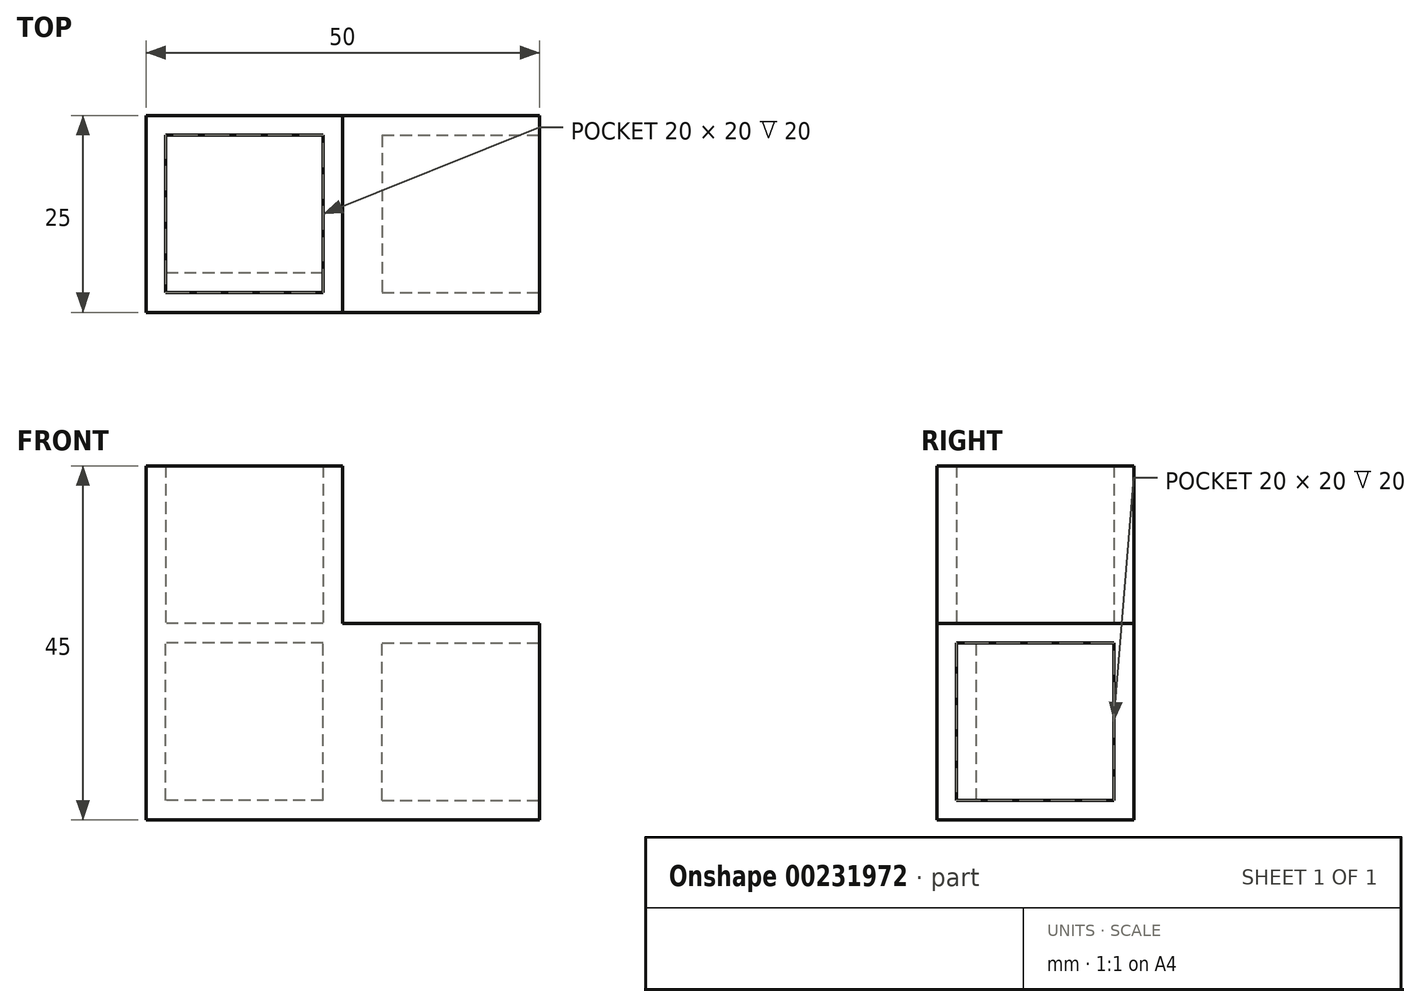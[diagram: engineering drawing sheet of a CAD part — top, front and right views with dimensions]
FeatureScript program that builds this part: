
annotation { "Feature Type Name" : "Feature", "Feature Type Description" : "" }
export const myFeature = defineFeature(function(context is Context, id is Id, definition is map)
    precondition{}
    {
        {
            var Q0;
            Q0=qCreatedBy(makeId("Top.planeOp"),FACE);
            var sketch = newSketch(context, id + "F0", { "sketchPlane" : qUnion([Q0])});
            skLineSegment(sketch, "E0.top", {"start": v(0, 30) * mm, "end": v(-25, 30) * mm});
            skLineSegment(sketch, "E0.left", {"start": v(0, 5) * mm, "end": v(0, 30) * mm});
            skLineSegment(sketch, "E0.right", {"start": v(-25, 5) * mm, "end": v(-25, 30) * mm});
            skLineSegment(sketch, "E1.top", {"start": v(0, 10) * mm, "end": v(-25, 10) * mm});
            skLineSegment(sketch, "E1.left", {"start": v(0, 5) * mm, "end": v(0, 10) * mm});
            skLineSegment(sketch, "E1.right", {"start": v(-25, 5) * mm, "end": v(-25, 10) * mm});
            skLineSegment(sketch, "E2.bottom", {"start": v(0, 30) * mm, "end": v(5, 30) * mm});
            skLineSegment(sketch, "E2.left", {"start": v(0, 30) * mm, "end": v(0, 5) * mm});
            skLineSegment(sketch, "E2.right", {"start": v(5, 30) * mm, "end": v(5, 5) * mm});
            skLineSegment(sketch, "E3.bottom", {"start": v(5, 30) * mm, "end": v(25, 30) * mm});
            skLineSegment(sketch, "E3.top", {"start": v(5, 5) * mm, "end": v(25, 5) * mm});
            skLineSegment(sketch, "E3.right", {"start": v(25, 30) * mm, "end": v(25, 5) * mm});
            skLineSegment(sketch, "E4", {"start": v(5, 5) * mm, "end": v(-25, 5) * mm});
            skSolve(sketch);
        }
        {
            var Q0;
            Q0=qSketchRegion(id+"F0",true);
            extrude(context, id + "F1", {"entities" : qUnion([Q0]), "depth" : 25 * mm});
        }
        {
            var Q0;
            Q0=makeQuery(id+"F1.opExtrude","SWEPT_FACE",FACE,{"disambiguationData":[OSD([sQuery(id+"F0.wireOp",EDGE,"E0.top"),sQuery(id+"F0.wireOp",EDGE,"E2.bottom"),sQuery(id+"F0.wireOp",EDGE,"E3.bottom")])]});
            var sketch = newSketch(context, id + "F2", { "sketchPlane" : qUnion([Q0])});
            skLineSegment(sketch, "E5.bottom", {"start": v(25, 25) * mm, "end": v(0, 25) * mm});
            skLineSegment(sketch, "E5.top", {"start": v(25, 0) * mm, "end": v(0, 0) * mm});
            skLineSegment(sketch, "E5.left", {"start": v(25, 25) * mm, "end": v(25, 0) * mm});
            skLineSegment(sketch, "E5.right", {"start": v(0, 25) * mm, "end": v(0, 0) * mm});
            skLineSegment(sketch, "E6.bottom", {"start": v(2.5, 2.5) * mm, "end": v(22.5, 2.5) * mm});
            skLineSegment(sketch, "E6.top", {"start": v(2.5, 22.5) * mm, "end": v(22.5, 22.5) * mm});
            skLineSegment(sketch, "E6.left", {"start": v(2.5, 2.5) * mm, "end": v(2.5, 22.5) * mm});
            skLineSegment(sketch, "E6.right", {"start": v(22.5, 2.5) * mm, "end": v(22.5, 22.5) * mm});
            skPoint(sketch, "E6.middle", {"position": v(12.5, 12.5) * mm});
            skPoint(sketch, "E6.middle.positionSnap0", {"position": v(25, 12.5) * mm});
            skPoint(sketch, "E6.middle.positionSnap1", {"position": v(12.5, 25) * mm});
            skPoint(sketch, "E6.centerSnap0", {"position": v(25, 12.5) * mm});
            skPoint(sketch, "E6.centerSnap1", {"position": v(12.5, 25) * mm});
            skSolve(sketch);
        }
        {
            var Q0;
            Q0=makeQuery(id+"F2.imprint","IMPRINT",FACE,{"disambiguationData":[TD([[makeQuery(id+"F2.imprint","IMPRINT",EDGE,{"derivedFrom":sQuery(id+"F2.wireOp",EDGE,"E6.bottom")}),1.0]])]});
            extrude(context, id + "F3", {"entities" : qUnion([Q0]), "operationType" : NewBodyOperationType.REMOVE, "oppositeDirection" : true, "depth" : 20 * mm});
        }
        {
            var Q0;
            Q0=makeQuery(id+"F1.opExtrude","SWEPT_FACE",FACE,{"disambiguationData":[OSD([sQuery(id+"F0.wireOp",EDGE,"E3.right")])]});
            var sketch = newSketch(context, id + "F4", { "sketchPlane" : qUnion([Q0])});
            skLineSegment(sketch, "E7.bottom", {"start": v(5, 0) * mm, "end": v(30, 0) * mm});
            skLineSegment(sketch, "E7.top", {"start": v(5, 25) * mm, "end": v(30, 25) * mm});
            skLineSegment(sketch, "E7.left", {"start": v(5, 0) * mm, "end": v(5, 25) * mm});
            skLineSegment(sketch, "E7.right", {"start": v(30, 0) * mm, "end": v(30, 25) * mm});
            skLineSegment(sketch, "E8.bottom", {"start": v(27.5, 2.5) * mm, "end": v(7.5, 2.5) * mm});
            skLineSegment(sketch, "E8.top", {"start": v(27.5, 22.5) * mm, "end": v(7.5, 22.5) * mm});
            skLineSegment(sketch, "E8.left", {"start": v(27.5, 2.5) * mm, "end": v(27.5, 22.5) * mm});
            skLineSegment(sketch, "E8.right", {"start": v(7.5, 2.5) * mm, "end": v(7.5, 22.5) * mm});
            skPoint(sketch, "E8.middle", {"position": v(17.5, 12.5) * mm});
            skPoint(sketch, "E8.middle.positionSnap0", {"position": v(17.5, 25) * mm});
            skPoint(sketch, "E8.middle.positionSnap1", {"position": v(5, 12.5) * mm});
            skPoint(sketch, "E8.centerSnap0", {"position": v(17.5, 25) * mm});
            skPoint(sketch, "E8.centerSnap1", {"position": v(5, 12.5) * mm});
            skSolve(sketch);
        }
        {
            var Q0;
            Q0=makeQuery(id+"F4.imprint","IMPRINT",FACE,{"disambiguationData":[TD([[makeQuery(id+"F4.imprint","IMPRINT",EDGE,{"derivedFrom":sQuery(id+"F4.wireOp",EDGE,"E8.bottom")}),-1.0]])]});
            extrude(context, id + "F5", {"entities" : qUnion([Q0]), "operationType" : NewBodyOperationType.REMOVE, "oppositeDirection" : true, "depth" : 20 * mm});
        }
        {
            var Q0;
            Q0=makeQuery(id+"F1.opExtrude","CAP_FACE",FACE,{"disambiguationData":[OSD([sQuery(id+"F0.wireOp",EDGE,"E0.top"),sQuery(id+"F0.wireOp",EDGE,"E0.right"),sQuery(id+"F0.wireOp",EDGE,"E1.bottom"),sQuery(id+"F0.wireOp",EDGE,"E1.right"),sQuery(id+"F0.wireOp",EDGE,"E2.bottom"),sQuery(id+"F0.wireOp",EDGE,"E2.top"),sQuery(id+"F0.wireOp",EDGE,"E2.right"),sQuery(id+"F0.wireOp",EDGE,"E3.bottom"),sQuery(id+"F0.wireOp",EDGE,"E3.top"),sQuery(id+"F0.wireOp",EDGE,"E3.right")])],"isStart":false});
            var sketch = newSketch(context, id + "F6", { "sketchPlane" : qUnion([Q0])});
            skLineSegment(sketch, "E9.bottom", {"start": v(-25, 30) * mm, "end": v(0, 30) * mm});
            skLineSegment(sketch, "E9.top", {"start": v(-25, 5) * mm, "end": v(0, 5) * mm});
            skLineSegment(sketch, "E9.left", {"start": v(-25, 30) * mm, "end": v(-25, 5) * mm});
            skLineSegment(sketch, "E9.right", {"start": v(0, 30) * mm, "end": v(0, 5) * mm});
            skLineSegment(sketch, "E10.bottom", {"start": v(-2.5, 7.5) * mm, "end": v(-22.5, 7.5) * mm});
            skLineSegment(sketch, "E10.top", {"start": v(-2.5, 27.5) * mm, "end": v(-22.5, 27.5) * mm});
            skLineSegment(sketch, "E10.left", {"start": v(-2.5, 7.5) * mm, "end": v(-2.5, 27.5) * mm});
            skLineSegment(sketch, "E10.right", {"start": v(-22.5, 7.5) * mm, "end": v(-22.5, 27.5) * mm});
            skPoint(sketch, "E10.middle", {"position": v(-12.5, 17.5) * mm});
            skPoint(sketch, "E10.middle.positionSnap0", {"position": v(-25, 17.5) * mm});
            skPoint(sketch, "E10.middle.positionSnap1", {"position": v(-12.5, 30) * mm});
            skPoint(sketch, "E10.centerSnap0", {"position": v(-25, 17.5) * mm});
            skPoint(sketch, "E10.centerSnap1", {"position": v(-12.5, 30) * mm});
            skSolve(sketch);
        }
        {
            var Q0;
            Q0=qSketchRegion(id+"F6",true);
            extrude(context, id + "F7", {"entities" : qUnion([Q0]), "operationType" : NewBodyOperationType.ADD, "depth" : 20 * mm});
        }
    });
